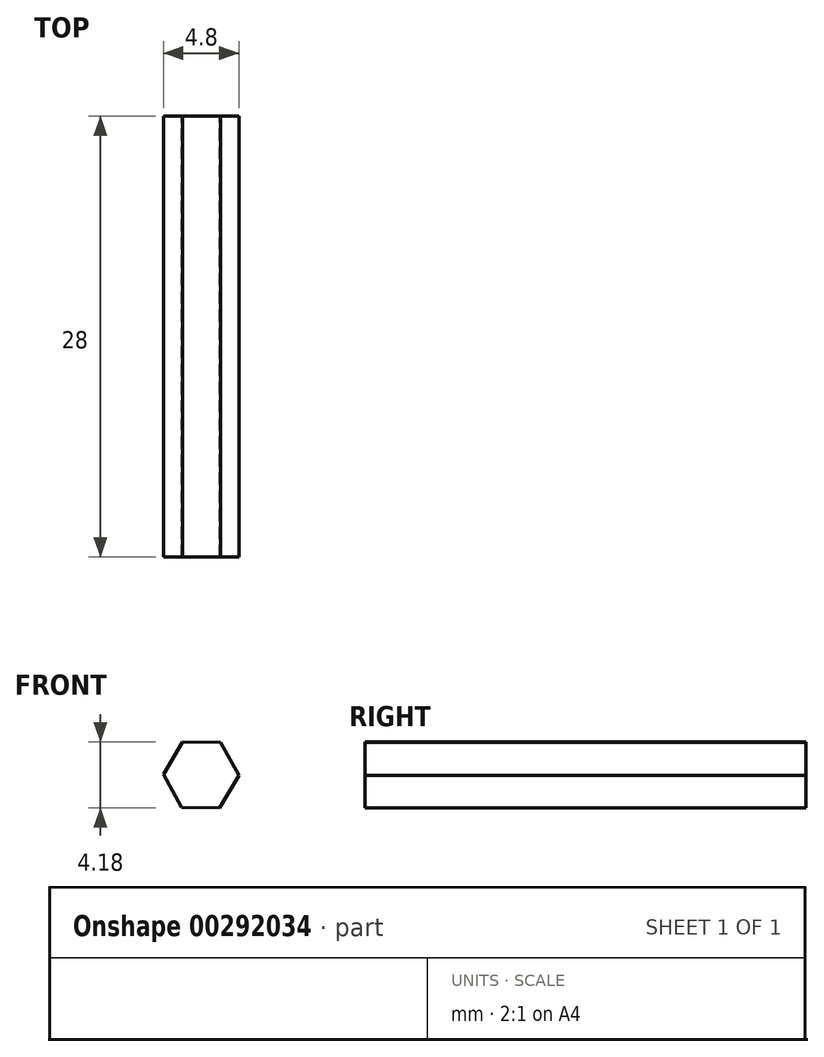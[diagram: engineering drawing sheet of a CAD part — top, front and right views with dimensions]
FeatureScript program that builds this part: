
annotation { "Feature Type Name" : "Feature", "Feature Type Description" : "" }
export const myFeature = defineFeature(function(context is Context, id is Id, definition is map)
    precondition{}
    {
        {
            var Q0;
            Q0=qCreatedBy(makeId("Front.planeOp"),FACE);
            var sketch = newSketch(context, id + "F0", { "sketchPlane" : qUnion([Q0])});
            skCircle(sketch, "E0.cCircle", {"center": v(0, 0) * mm, "radius": 2.08 * mm, "construction": true});
            skLineSegment(sketch, "E0.0", {"start": v(1.23, 2.06) * mm, "end": v(2.4, -0.03) * mm});
            skLineSegment(sketch, "E0.1", {"start": v(2.4, -0.03) * mm, "end": v(1.17, -2.1) * mm});
            skLineSegment(sketch, "E0.2", {"start": v(1.17, -2.1) * mm, "end": v(-1.23, -2.06) * mm});
            skLineSegment(sketch, "E0.3", {"start": v(-1.23, -2.06) * mm, "end": v(-2.4, 0.03) * mm});
            skLineSegment(sketch, "E0.4", {"start": v(-2.4, 0.03) * mm, "end": v(-1.17, 2.1) * mm});
            skLineSegment(sketch, "E0.5", {"start": v(-1.17, 2.1) * mm, "end": v(1.23, 2.06) * mm});
            skPoint(sketch, "E0.0.midPoint", {"position": v(1.81, 1.01) * mm});
            skSolve(sketch);
        }
        {
            var Q0;
            Q0 = qSketchRegion(id + "F0", true);
            extrude(context, id + "F1", {"entities" : qUnion([Q0]), "depth" : 28 * mm});
        }
    });
